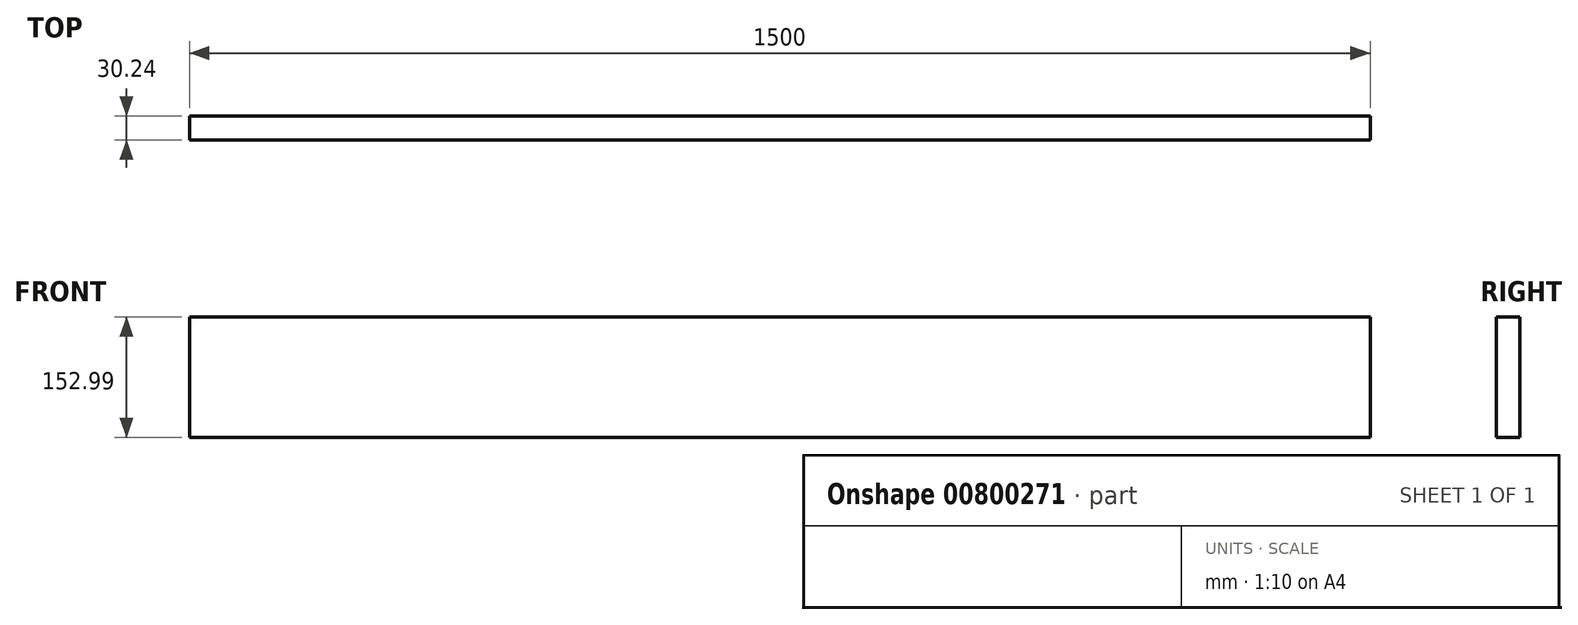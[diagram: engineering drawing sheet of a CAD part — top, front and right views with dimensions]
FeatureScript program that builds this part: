
annotation { "Feature Type Name" : "Feature", "Feature Type Description" : "" }
export const myFeature = defineFeature(function(context is Context, id is Id, definition is map)
    precondition{}
    {
        {
            var Q0;
            Q0=qCreatedBy(makeId("Right.planeOp"),FACE);
            var sketch = newSketch(context, id + "F0", { "sketchPlane" : qUnion([Q0])});
            skLineSegment(sketch, "E0.bottom", {"start": v(-66.38, 0) * mm, "end": v(-59.14, 0) * mm});
            skLineSegment(sketch, "E0.top", {"start": v(-66.38, -23) * mm, "end": v(-59.14, -23) * mm});
            skLineSegment(sketch, "E0.left", {"start": v(-66.38, 0) * mm, "end": v(-66.38, -23) * mm});
            skLineSegment(sketch, "E0.right", {"start": v(-59.14, 0) * mm, "end": v(-59.14, -23) * mm});
            skSolve(sketch);
        }
        {
            var Q0;
            Q0 = qSketchRegion(id + "F0", true);
            extrude(context, id + "F1", {"entities" : qUnion([Q0]), "depth" : 1500 * mm, "offsetDistance" : 25 * mm});
        }
        {
            var Q0;
            Q0=makeQuery(id+"F1.opExtrude","SWEPT_FACE",FACE,{"disambiguationData":[OSD([sQuery(id+"F0.wireOp",EDGE,"E0.top")])]});
            extrude(context, id + "F2", {"entities" : qUnion([Q0]), "operationType" : NewBodyOperationType.ADD, "depth" : 130 * mm, "offsetDistance" : 25 * mm});
        }
        {
            var Q0;
            {var subQ0=sQuery(id+"F0.wireOp",EDGE,"E0.left");Q0=makeQuery(id+"F2.boolean.opBoolean","MERGE",FACE,{"derivedFrom":[makeQuery(id+"F1.opExtrude","SWEPT_FACE",FACE,{"disambiguationData":[OSD([subQ0])]}),makeQuery(id+"F2.opExtrude","SWEPT_FACE",FACE,{"disambiguationData":[OSD([sQuery(id+"F0.wireOp",EDGE,"E0.top"),subQ0])]})]});}
            extrude(context, id + "F3", {"entities" : qUnion([Q0]), "operationType" : NewBodyOperationType.ADD, "depth" : 23 * mm, "offsetDistance" : 25 * mm});
        }
    });
